# Revit family: Structures Unlimited Center Ridge Canopy
name_source: partatom
category: Generic Models
revit_build: Autodesk Revit 2018 (Build: 20170223_1515(x64)
units: mm (PartAtom-declared; Revit-internal decimal feet)

## family parameters
Always vertical = Yes
Can host rebar = No
Cut with Voids When Loaded = No
Part Type = Normal
Room Calculation Point = No
Round Connector Dimension = Use Diameter
Shared = Yes
Work Plane-Based = No

## types (13) — shared parameters
Manufacturer = Structures Unlimited, Inc.
Model = Center Ridge Canopy
URL = https://www.structuresunlimitedinc.com

## type names (no varying parameters)
- KCRF Aluminum #79
- KCRF Banner Red #90
- KCRF Black #95
- KCRF Blue #15
- KCRF Bone White #21B
- KCRF Brick #88
- KCRF Bronze #85
- KCRF Coro Blue #48
- KCRF Gray #80
- KCRF Hartford Green #75
- KCRF Minuette #03
- KCRF Mountain Green #70
- KCRF White #00

note: column(s) folded — value = type name in every type: KCRF

## geometry (parser evidence)
native form markers: Blend x2, Sweep x21
no freeform markers — native parametric forms only
